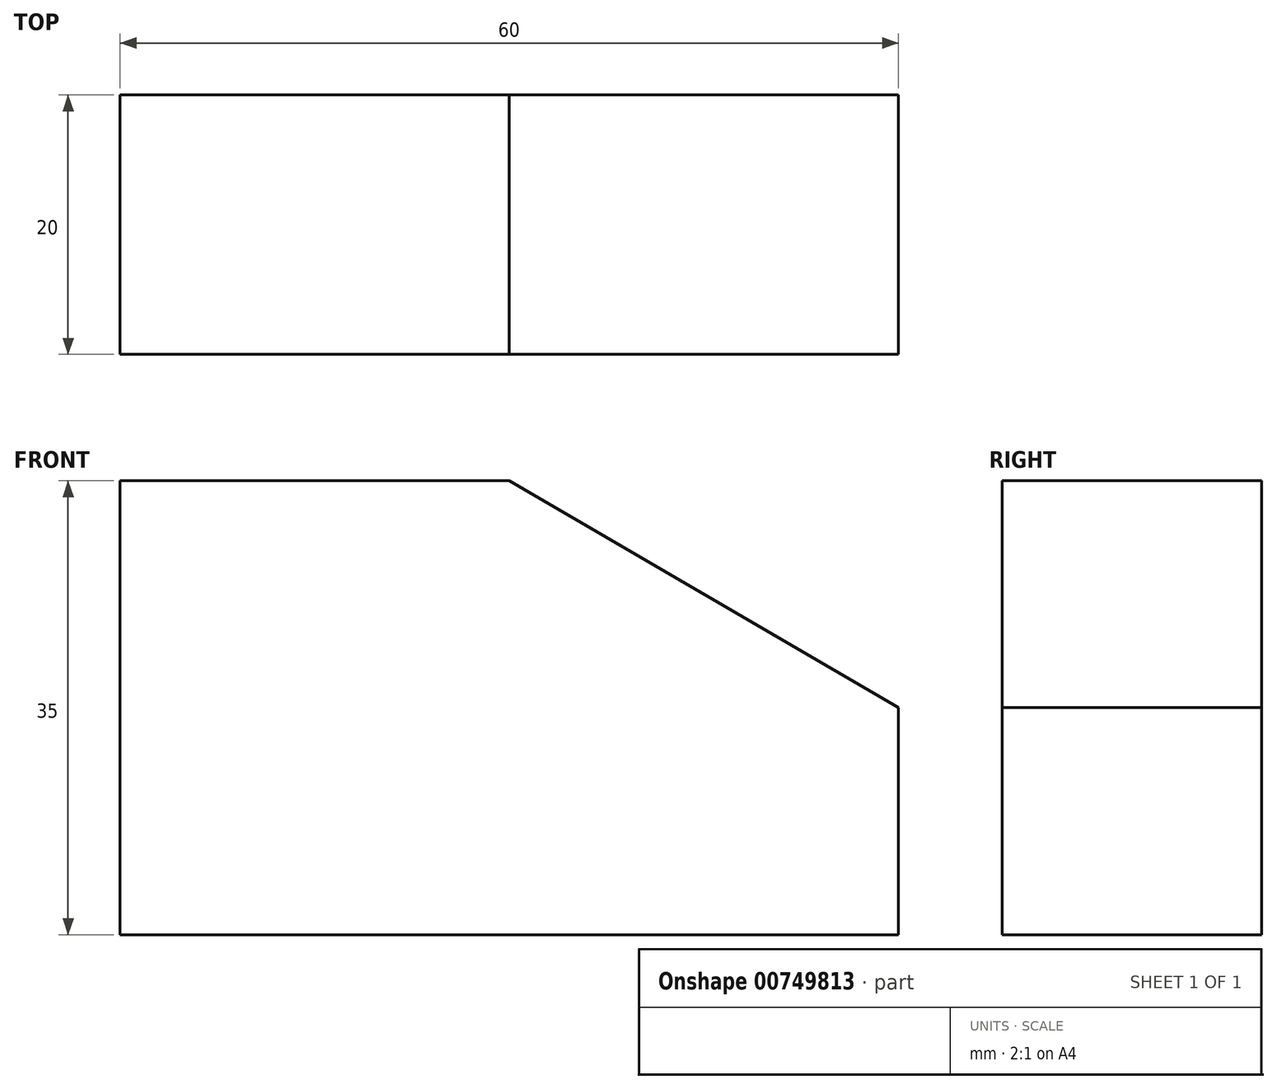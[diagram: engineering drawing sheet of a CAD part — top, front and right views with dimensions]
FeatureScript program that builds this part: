
annotation { "Feature Type Name" : "Feature", "Feature Type Description" : "" }
export const myFeature = defineFeature(function(context is Context, id is Id, definition is map)
    precondition{}
    {
        {
            var Q0;
            Q0=qCreatedBy(makeId("Front.planeOp"),FACE);
            var sketch = newSketch(context, id + "F0", { "sketchPlane" : qUnion([Q0])});
            skLineSegment(sketch, "E0", {"start": v(0, 0) * mm, "end": v(0, -35) * mm});
            skLineSegment(sketch, "E1", {"start": v(0, -35) * mm, "end": v(60, -35) * mm});
            skLineSegment(sketch, "E2", {"start": v(60, -35) * mm, "end": v(60, -17.5) * mm});
            skLineSegment(sketch, "E3", {"start": v(60, -17.5) * mm, "end": v(30, 0) * mm});
            skLineSegment(sketch, "E4", {"start": v(30, 0) * mm, "end": v(0, 0) * mm});
            skSolve(sketch);
        }
        {
            var Q0;
            Q0=makeQuery(id+"F0.imprint","IMPRINT",FACE,{"disambiguationData":[TD([[makeQuery(id+"F0.imprint","IMPRINT",EDGE,{"derivedFrom":sQuery(id+"F0.wireOp",EDGE,"E0")}),1.0]])]});
            extrude(context, id + "F1", {"entities" : qUnion([Q0]), "depth" : 20 * mm, "offsetDistance" : 25 * mm});
        }
    });
